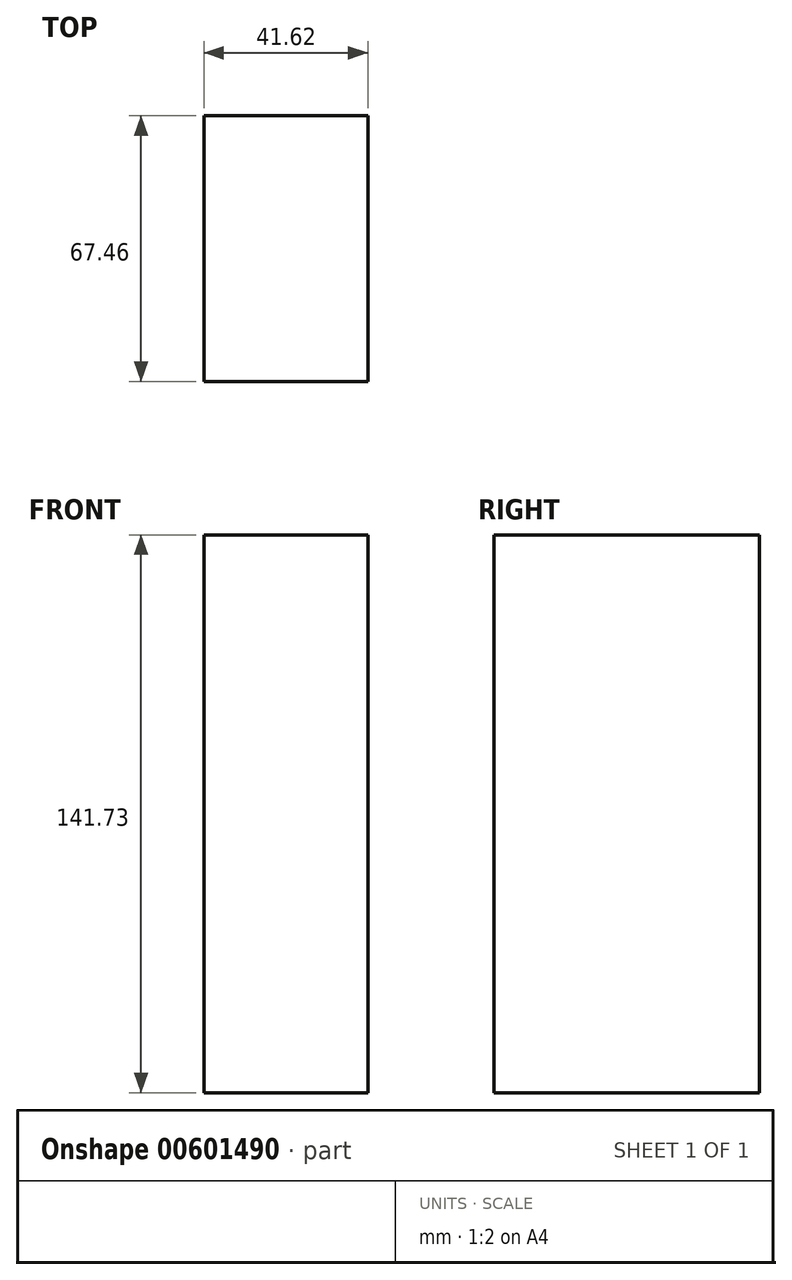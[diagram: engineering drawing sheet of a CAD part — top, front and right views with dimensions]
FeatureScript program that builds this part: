
annotation { "Feature Type Name" : "Feature", "Feature Type Description" : "" }
export const myFeature = defineFeature(function(context is Context, id is Id, definition is map)
    precondition{}
    {
        {
            var Q0;
            Q0=qCreatedBy(makeId("Top.planeOp"),FACE);
            var sketch = newSketch(context, id + "F0", { "sketchPlane" : qUnion([Q0])});
            skLineSegment(sketch, "E0.bottom", {"start": v(-36.79, 63.1) * mm, "end": v(4.83, 63.1) * mm});
            skLineSegment(sketch, "E0.top", {"start": v(-36.79, -4.36) * mm, "end": v(4.83, -4.36) * mm});
            skLineSegment(sketch, "E0.left", {"start": v(-36.79, 63.1) * mm, "end": v(-36.79, -4.36) * mm});
            skLineSegment(sketch, "E0.right", {"start": v(4.83, 63.1) * mm, "end": v(4.83, -4.36) * mm});
            skSolve(sketch);
        }
        {
            var Q0;
            Q0=makeQuery(id+"F0.imprint","IMPRINT",FACE,{"disambiguationData":[TD([[makeQuery(id+"F0.imprint","IMPRINT",EDGE,{"derivedFrom":sQuery(id+"F0.wireOp",EDGE,"E0.bottom")}),-1.0]])]});
            extrude(context, id + "F1", {"entities" : qUnion([Q0]), "depth" : 141.73 * mm, "offsetDistance" : 25.4 * mm});
        }
    });
